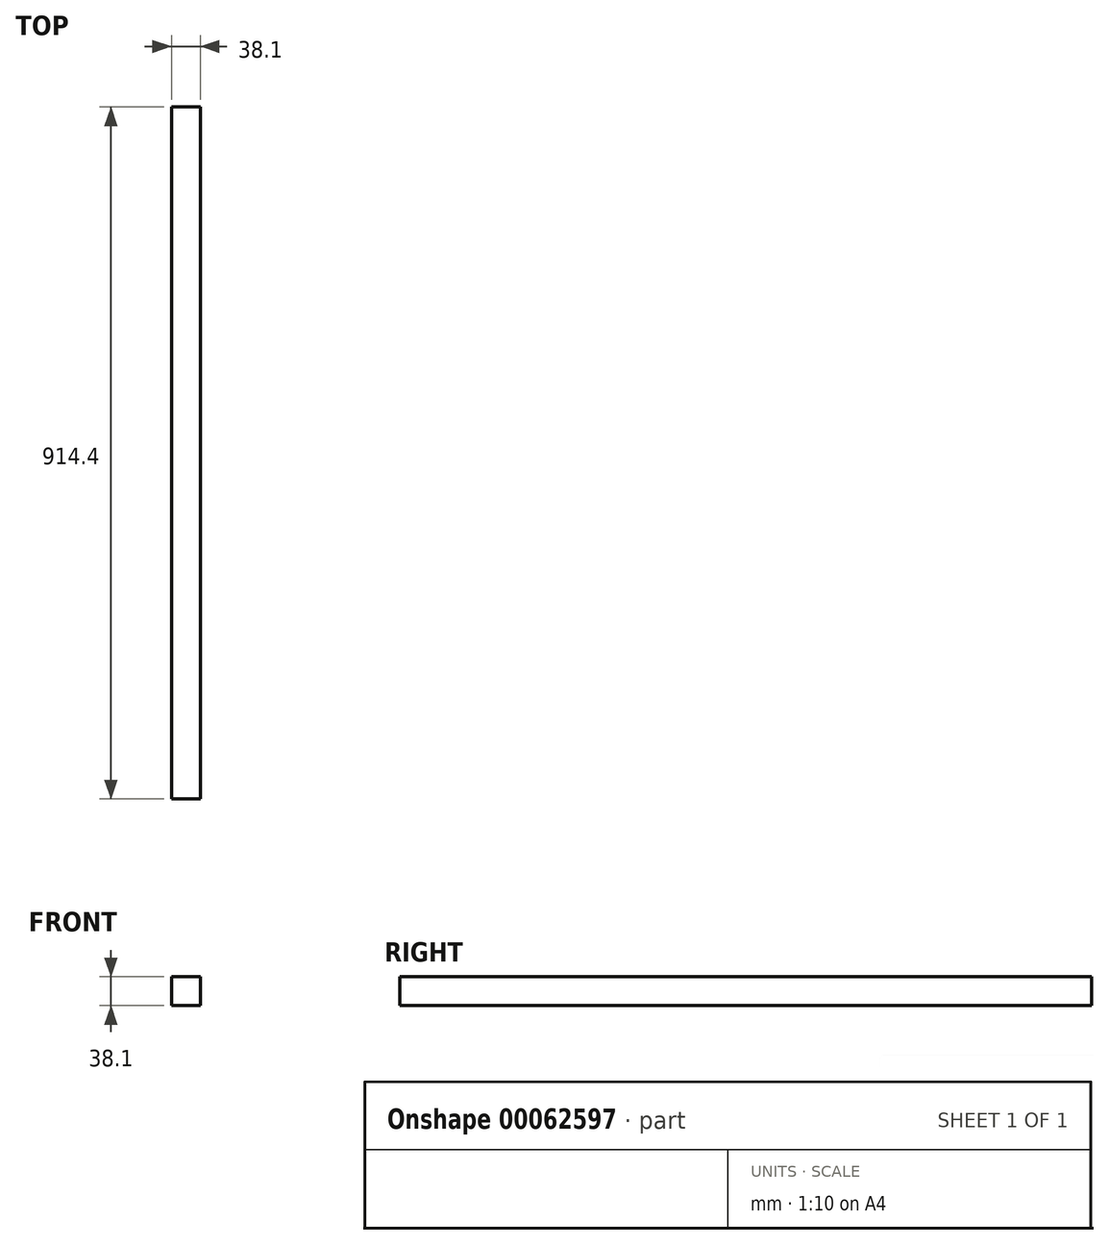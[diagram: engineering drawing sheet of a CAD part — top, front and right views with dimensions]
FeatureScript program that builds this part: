
annotation { "Feature Type Name" : "Feature", "Feature Type Description" : "" }
export const myFeature = defineFeature(function(context is Context, id is Id, definition is map)
    precondition{}
    {
        {
            var Q0;
            Q0=qCreatedBy(makeId("Front.planeOp"),FACE);
            var sketch = newSketch(context, id + "F0", { "sketchPlane" : qUnion([Q0])});
            skLineSegment(sketch, "E0.bottom", {"start": v(0, 0) * mm, "end": v(38.1, 0) * mm});
            skLineSegment(sketch, "E0.top", {"start": v(0, 38.1) * mm, "end": v(38.1, 38.1) * mm});
            skLineSegment(sketch, "E0.left", {"start": v(0, 0) * mm, "end": v(0, 38.1) * mm});
            skLineSegment(sketch, "E0.right", {"start": v(38.1, 0) * mm, "end": v(38.1, 38.1) * mm});
            skSolve(sketch);
        }
        {
            var Q0;
            Q0=makeQuery(id+"F0.imprint","IMPRINT",FACE,{"disambiguationData":[TD([[makeQuery(id+"F0.imprint","IMPRINT",EDGE,{"derivedFrom":sQuery(id+"F0.wireOp",EDGE,"E0.bottom")}),1.0]])]});
            extrude(context, id + "F1", {"entities" : qUnion([Q0]), "depth" : 914.4 * mm});
        }
    });
